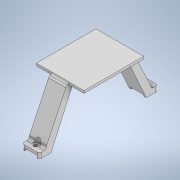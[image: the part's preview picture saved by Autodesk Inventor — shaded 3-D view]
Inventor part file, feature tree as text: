
AUTODESK INVENTOR PART (.ipt)
format: ipt  version: 2022 (Build 260153000, 153)  size: 305,664 bytes
history: native  units: in
note: dims shown in document units (in); Inventor stores cm internally (conversion verified against a paired STEP export)
features: sketch x8, extrude x7, fillet x3, hole x1
ambient origin geometry x8: Origin, YZ Plane, XZ Plane, XY Plane, X Axis, Y Axis, Z Axis, Center Point
bodies: Solid1 (feature_tree)
feature tree (19):
  extrude  "Extrusion1"  Depth=3.7559in
  extrude  "Extrusion2"  Depth=1.5748in
  fillet  "Fillet1"  Radius=1.9685in
  extrude  "Extrusion3"  Depth=0.502in
  hole  "Hole1"  [1 undecoded]
  fillet  "Fillet3"  Radius=0.1575in
  extrude  "Extrusion7"  Depth=0.1575in
  extrude  "Extrusion8"  Depth=0.4515in
  extrude  "Extrusion9"  TaperAngle=0.0deg  [1 undecoded]
  extrude  "Extrusion10"  Depth=0.0787in
  fillet  "Fillet5"  Radius=0.0787in
  sketch  "Sketch1"  dims[d0=0.5709in d1=3.7559in]
  sketch  "Sketch2"  dims[d2=1.6535in d3=0.0in d4=1.5748in d5=1.9685in]
  sketch  "Sketch3"  dims[d6=0.8937in d7=0.502in]
  sketch  "Sketch4"  dims[d8=0.0787in d9=0.0in d10=0.0787in d11=0.1575in]
  sketch  "Sketch8"  dims[d12=1.378in d13=0.1575in]
  sketch  "Sketch10"  dims[d14=1.378in d15=0.4515in]
  sketch  "Sketch11"  dims[d16=0.7853in d17=0.0in d18=0.0in]
  sketch  "Sketch12"  dims[d19=0.1181in d20=0.2362in d21=0.1181in d22=0.0394in d23=90.0deg d24=0.315in d25=0.8108in d33=0.0984in d38=0.0787in d39=0.0in d40=0.0787in d41=0.0in d42=0.4134in d43=0.0787in d44=0.0787in d45=0.1969in d46=0.0in d47=0.0in d49=0.2362in d50=0.2362in d51=0.1969in d52=0.0in d53=0.0787in d54=3.1496in d55=0.3031in]
note: 2 required parameter values undecoded (feature->parameter linkage not recoverable at this tier; creation-order binding heuristic only, values carry confidence <= 0.55)
